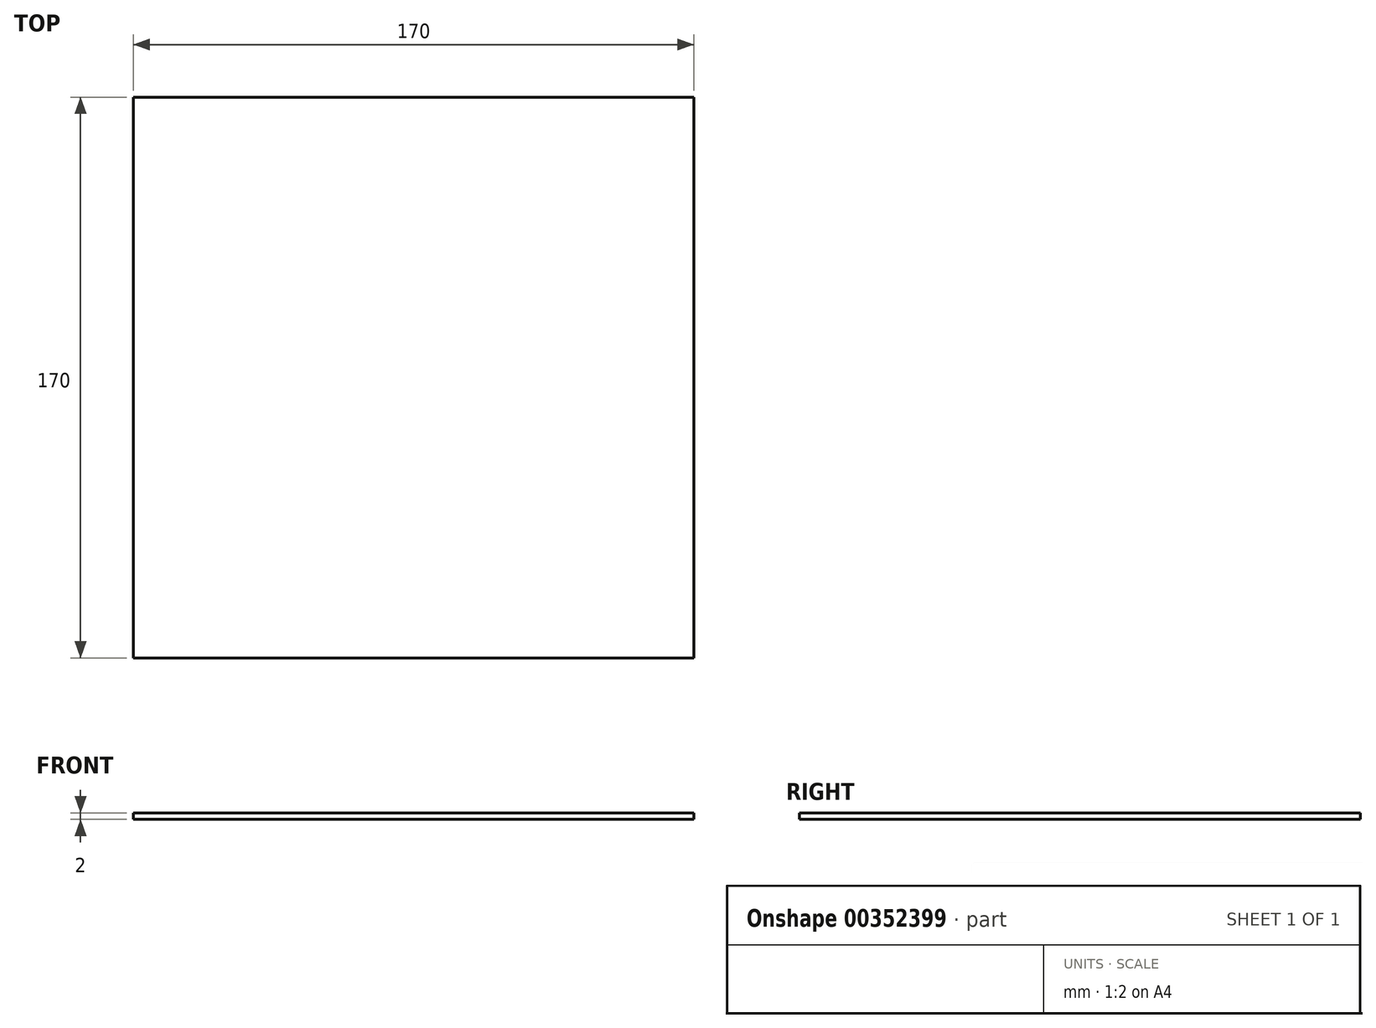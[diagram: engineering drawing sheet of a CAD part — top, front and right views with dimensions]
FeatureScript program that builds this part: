
annotation { "Feature Type Name" : "Feature", "Feature Type Description" : "" }
export const myFeature = defineFeature(function(context is Context, id is Id, definition is map)
    precondition{}
    {
        {
            var Q0;
            Q0=qCreatedBy(makeId("Top.planeOp"),FACE);
            var sketch = newSketch(context, id + "F0", { "sketchPlane" : qUnion([Q0])});
            skLineSegment(sketch, "E0.bottom", {"start": v(0, 0) * mm, "end": v(170, 0) * mm});
            skLineSegment(sketch, "E0.top", {"start": v(0, 170) * mm, "end": v(170, 170) * mm});
            skLineSegment(sketch, "E0.left", {"start": v(0, 0) * mm, "end": v(0, 170) * mm});
            skLineSegment(sketch, "E0.right", {"start": v(170, 0) * mm, "end": v(170, 170) * mm});
            skSolve(sketch);
        }
        {
            var Q0;
            Q0=makeQuery(id+"F0.imprint","IMPRINT",FACE,{"disambiguationData":[TD([[makeQuery(id+"F0.imprint","IMPRINT",EDGE,{"derivedFrom":sQuery(id+"F0.wireOp",EDGE,"E0.bottom")}),1.0]])]});
            extrude(context, id + "F1", {"entities" : qUnion([Q0]), "depth" : 2 * mm});
        }
    });
